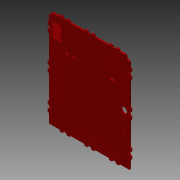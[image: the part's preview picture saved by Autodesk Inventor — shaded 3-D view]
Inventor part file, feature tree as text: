
AUTODESK INVENTOR PART (.ipt)
format: ipt  version: 2013 (Build 170138000, 138)  size: 671,744 bytes
history: native  units: mm
features: extrude x3, sketch x3
ambient origin geometry x8: Origin, YZ Plane, XZ Plane, XY Plane, X Axis, Y Axis, Z Axis, Center Point
bodies: Solid1 (feature_tree)
feature tree (6):
  extrude  "Extrusion1"  Depth=102.286672mm
  extrude  "Extrusion2"  Depth=6.0mm TaperAngle=0.0deg
  extrude  "Extrusion3"  Depth=6.0mm
  sketch  "Sketch1"  dims[d0=171.789163mm d1=102.286672mm]
  sketch  "Sketch2"  dims[d2=395.2mm d4=6.0mm d5=0.0mm]
  sketch  "Sketch3"  dims[d6=6.0mm d54=6.0mm d55=6.0mm d56=16.0mm d57=11.0mm d58=7.0mm d59=1.8mm d60=1.8mm d62=11.8mm d63=12.4mm d64=0.3mm d65=6.1mm d66=6.1mm d67=3.0mm d68=1.25mm d69=1.25mm d70=12.4mm d71=100.0mm d72=6.1mm d73=12.4mm d74=3.0mm d75=1.25mm d76=1.25mm d77=100.0mm d78=6.1mm d79=12.4mm d80=6.1mm d81=12.4mm d82=3.0mm d83=1.25mm d84=1.25mm d85=6.1mm d86=11.8mm d87=10.6mm d88=1.8mm d89=1.8mm d90=6.0mm d92=12.4mm d93=6.1mm d94=3.0mm d95=6.1mm d96=12.4mm d97=1.25mm d98=1.25mm d99=10.6mm d100=7.0mm d101=1.8mm d102=140.0mm d103=6.1mm d104=12.4mm d105=6.1mm d106=12.4mm d107=3.0mm d108=1.25mm d109=1.25mm d110=140.0mm d111=6.1mm d112=12.4mm d113=6.1mm d114=3.0mm d115=12.4mm d116=1.25mm d117=1.25mm d118=7.0mm d119=1.8mm d120=1.8mm d121=3.0mm d122=1.9mm d123=1.7mm d124=19.0mm d126=25.0mm d127=6.0mm d128=6.0mm d129=15.5mm d130=8.5mm d131=15.5mm d132=6.0mm d133=6.0mm d134=22.0mm d135=80.0mm d136=7.9mm d137=80.0mm d138=11.0mm d139=11.0mm d140=11.0mm d141=11.0mm d144=3.0mm d146=3.0mm d147=3.0mm d148=22.0mm d149=3.0mm d150=3.0mm d152=6.0mm d153=0.0mm d154=1.45mm d155=48.8mm d156=6.4mm d157=3.2mm d158=17.6mm d159=63.882mm d160=78.195mm d161=12.0mm d162=7.8mm d163=7.8mm d164=12.0mm d165=6.0mm d166=40.0mm d167=7.0mm d169=110.0mm d172=6.0mm d173=12.2mm d174=45.0mm d175=32.0mm d176=1.4mm d177=31.4mm d178=3.0mm d179=3.0mm d180=3.0mm d181=3.0mm d182=3.0mm d183=3.0mm d184=3.0mm d185=3.0mm d186=3.0mm d187=3.0mm d188=3.0mm d189=3.0mm d190=3.0mm d191=3.0mm d192=3.0mm d193=3.0mm d194=3.0mm d195=3.0mm d196=3.0mm d197=15.0mm d198=6.0mm d199=73.8mm d200=95.0mm d201=1.5mm d202=197.6mm d203=325.3mm d204=161.15mm d205=32.0mm d206=62.168mm d207=24.0mm d210=10.0mm d211=0.0mm d212=85.09mm d213=3.0mm d215=11.5mm d216=57.912mm d217=3.0mm d218=73.406mm]
